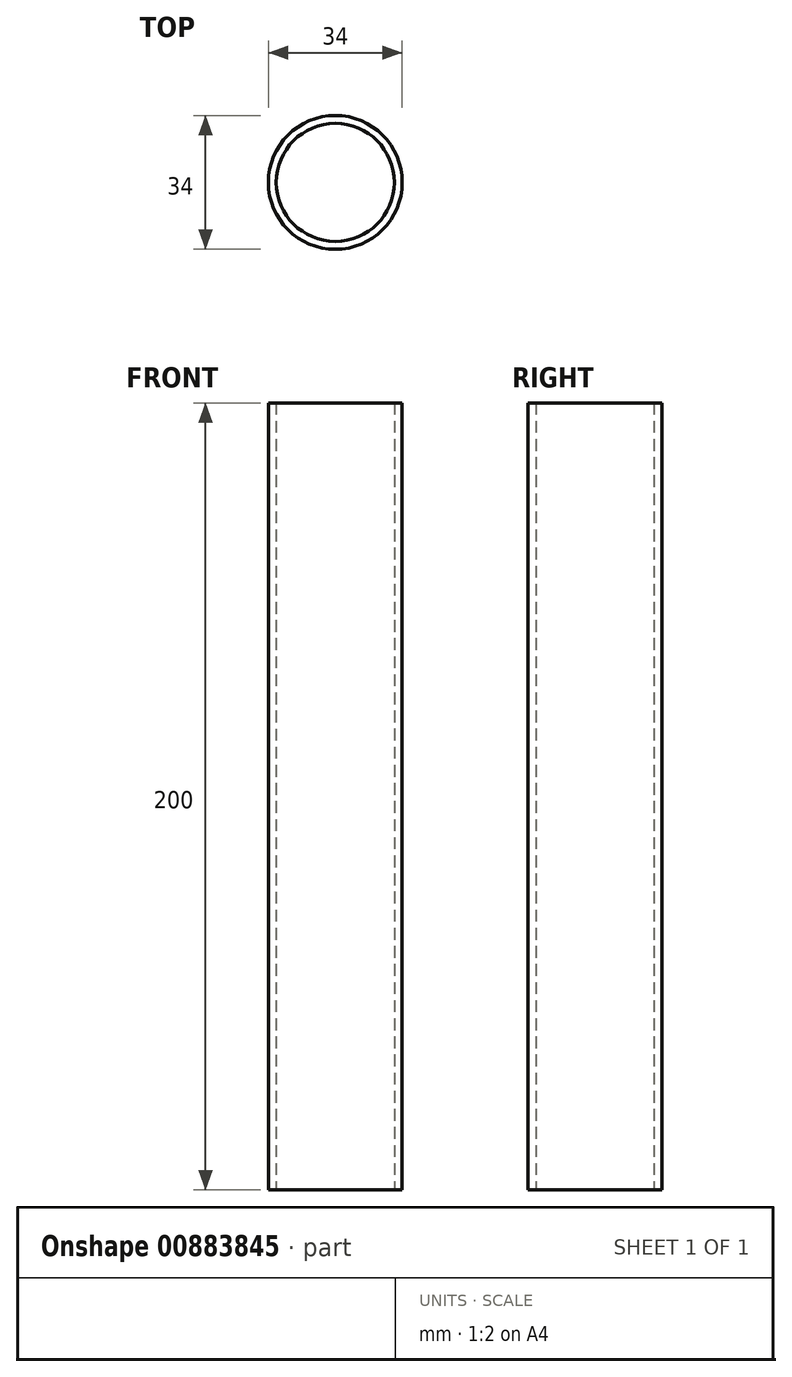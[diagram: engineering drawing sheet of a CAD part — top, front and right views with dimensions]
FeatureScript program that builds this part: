
annotation { "Feature Type Name" : "Feature", "Feature Type Description" : "" }
export const myFeature = defineFeature(function(context is Context, id is Id, definition is map)
    precondition{}
    {
        {
            var Q0;
            Q0=qCreatedBy(makeId("Front.planeOp"),FACE);
            var sketch = newSketch(context, id + "F0", { "sketchPlane" : qUnion([Q0])});
            skLineSegment(sketch, "E0", {"start": v(0, 0) * mm, "end": v(0, 201.64) * mm, "construction": true});
            skLineSegment(sketch, "E1.bottom", {"start": v(15, 0) * mm, "end": v(17, 0) * mm});
            skLineSegment(sketch, "E1.top", {"start": v(15, 200) * mm, "end": v(17, 200) * mm});
            skLineSegment(sketch, "E1.left", {"start": v(15, 0) * mm, "end": v(15, 200) * mm});
            skLineSegment(sketch, "E1.right", {"start": v(17, 0) * mm, "end": v(17, 200) * mm});
            skSolve(sketch);
        }
        {
            var Q0;
            Q0=makeQuery(id+"F0.imprint","IMPRINT",FACE,{"disambiguationData":[TD([[makeQuery(id+"F0.imprint","IMPRINT",EDGE,{"derivedFrom":sQuery(id+"F0.wireOp",EDGE,"E1.bottom")}),1.0]])]});
            var Q1;
            Q1=sQuery(id+"F0.wireOp",EDGE,"E0");
            revolve(context, id + "F1", {"surfaceOperationType" : NewSurfaceOperationType.NEW, "entities" : qUnion([Q0]), "axis" : qUnion([Q1]), "revolveType" : RevolveType.FULL});
        }
    });
